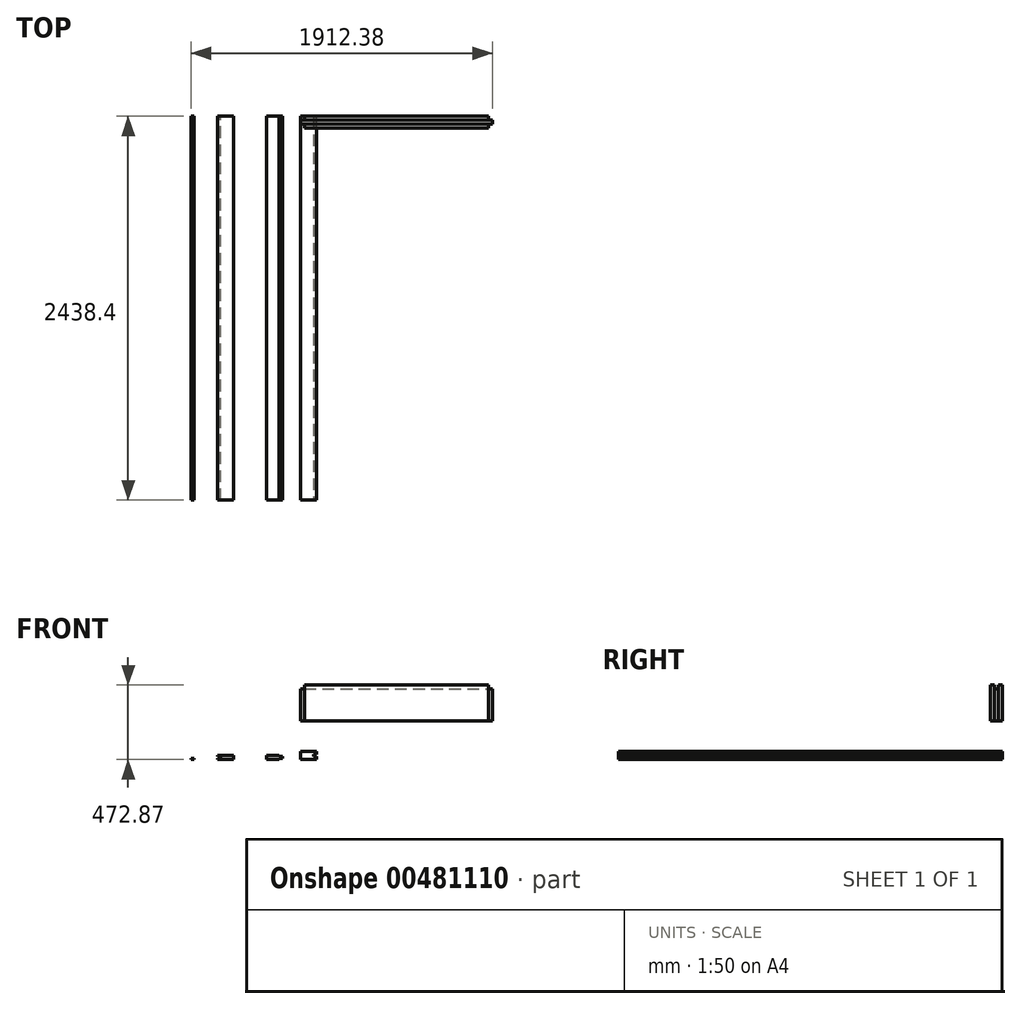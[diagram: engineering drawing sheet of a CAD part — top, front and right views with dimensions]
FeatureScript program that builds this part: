
annotation { "Feature Type Name" : "Feature", "Feature Type Description" : "" }
export const myFeature = defineFeature(function(context is Context, id is Id, definition is map)
    precondition{}
    {
        {
            var Q0;
            Q0=qCreatedBy(makeId("Front.planeOp"),FACE);
            var sketch = newSketch(context, id + "F0", { "sketchPlane" : qUnion([Q0])});
            skLineSegment(sketch, "E0.bottom", {"start": v(0, 0) * mm, "end": v(101.6, 0) * mm});
            skLineSegment(sketch, "E0.top", {"start": v(0, 50.8) * mm, "end": v(101.6, 50.8) * mm});
            skLineSegment(sketch, "E0.left", {"start": v(0, 0) * mm, "end": v(0, 50.8) * mm});
            skLineSegment(sketch, "E0.right", {"start": v(101.6, 0) * mm, "end": v(101.6, 50.8) * mm});
            skSolve(sketch);
        }
        {
            var Q0;
            Q0=makeQuery(id+"F0.imprint","IMPRINT",FACE,{"disambiguationData":[TD([[makeQuery(id+"F0.imprint","IMPRINT",EDGE,{"derivedFrom":sQuery(id+"F0.wireOp",EDGE,"E0.bottom")}),1.0]])]});
            extrude(context, id + "F1", {"entities" : qUnion([Q0]), "depth" : 2438.4 * mm});
        }
        {
            var Q0;
            Q0=makeQuery(id+"F1.opExtrude","SWEPT_FACE",FACE,{"disambiguationData":[OSD([sQuery(id+"F0.wireOp",EDGE,"E0.right")])]});
            var sketch = newSketch(context, id + "F2", { "sketchPlane" : qUnion([Q0])});
            skLineSegment(sketch, "E1.bottom", {"start": v(0, 19.05) * mm, "end": v(-2438.4, 19.05) * mm});
            skLineSegment(sketch, "E1.top", {"start": v(0, 31.75) * mm, "end": v(-2438.4, 31.75) * mm});
            skLineSegment(sketch, "E1.left", {"start": v(0, 19.05) * mm, "end": v(0, 31.75) * mm});
            skLineSegment(sketch, "E1.right", {"start": v(-2438.4, 19.05) * mm, "end": v(-2438.4, 31.75) * mm});
            skSolve(sketch);
        }
        {
            var Q0;
            Q0 = qSketchRegion(id + "F2", true);
            extrude(context, id + "F3", {"entities" : qUnion([Q0]), "operationType" : NewBodyOperationType.REMOVE, "oppositeDirection" : true, "depth" : 19.05 * mm});
        }
        {
            var Q0;
            Q0=qCreatedBy(makeId("Front.planeOp"),FACE);
            var sketch = newSketch(context, id + "F4", { "sketchPlane" : qUnion([Q0])});
            skLineSegment(sketch, "E2.bottom", {"start": v(-114.74, 0) * mm, "end": v(-216.34, 0) * mm});
            skLineSegment(sketch, "E2.top", {"start": v(-114.74, 25.4) * mm, "end": v(-216.34, 25.4) * mm});
            skLineSegment(sketch, "E2.left", {"start": v(-114.74, 0) * mm, "end": v(-114.74, 25.4) * mm});
            skLineSegment(sketch, "E2.right", {"start": v(-216.34, 0) * mm, "end": v(-216.34, 25.4) * mm});
            skSolve(sketch);
        }
        {
            var Q0;
            Q0 = qSketchRegion(id + "F4", true);
            extrude(context, id + "F5", {"entities" : qUnion([Q0]), "depth" : 2438.4 * mm});
        }
        {
            var Q0;
            Q0=makeQuery(id+"F5.opExtrude","CAP_FACE",FACE,{"disambiguationData":[OSD([sQuery(id+"F4.wireOp",EDGE,"E2.bottom"),sQuery(id+"F4.wireOp",EDGE,"E2.top"),sQuery(id+"F4.wireOp",EDGE,"E2.left"),sQuery(id+"F4.wireOp",EDGE,"E2.right")])],"isStart":false});
            var sketch = newSketch(context, id + "F6", { "sketchPlane" : qUnion([Q0])});
            skLineSegment(sketch, "E3.bottom", {"start": v(-114.74, 25.4) * mm, "end": v(-133.8, 25.4) * mm});
            skLineSegment(sketch, "E3.top", {"start": v(-114.74, 19.05) * mm, "end": v(-133.8, 19.05) * mm});
            skLineSegment(sketch, "E3.left", {"start": v(-114.74, 25.4) * mm, "end": v(-114.74, 19.05) * mm});
            skLineSegment(sketch, "E3.right", {"start": v(-133.8, 25.4) * mm, "end": v(-133.8, 19.05) * mm});
            skLineSegment(sketch, "E4.bottom", {"start": v(-114.74, 0) * mm, "end": v(-133.8, 0) * mm});
            skLineSegment(sketch, "E4.top", {"start": v(-114.74, 6.35) * mm, "end": v(-133.8, 6.35) * mm});
            skLineSegment(sketch, "E4.left", {"start": v(-114.74, 0) * mm, "end": v(-114.74, 6.35) * mm});
            skLineSegment(sketch, "E4.right", {"start": v(-133.8, 0) * mm, "end": v(-133.8, 6.35) * mm});
            skSolve(sketch);
        }
        {
            var Q0;
            Q0=makeQuery(id+"F6.imprint","IMPRINT",FACE,{"disambiguationData":[TD([[makeQuery(id+"F6.imprint","IMPRINT",EDGE,{"derivedFrom":sQuery(id+"F6.wireOp",EDGE,"E3.bottom")}),1.0]])]});
            var Q1;
            Q1=makeQuery(id+"F6.imprint","IMPRINT",FACE,{"disambiguationData":[TD([[makeQuery(id+"F6.imprint","IMPRINT",EDGE,{"derivedFrom":sQuery(id+"F6.wireOp",EDGE,"E4.bottom")}),-1.0]])]});
            extrude(context, id + "F7", {"entities" : qUnion([Q0, Q1]), "operationType" : NewBodyOperationType.REMOVE, "oppositeDirection" : true, "depth" : 2438.4 * mm});
        }
        {
            var Q0;
            Q0=qCreatedBy(makeId("Front.planeOp"),FACE);
            var sketch = newSketch(context, id + "F8", { "sketchPlane" : qUnion([Q0])});
            skLineSegment(sketch, "E5.bottom", {"start": v(-423.34, 0) * mm, "end": v(-524.94, 0) * mm});
            skLineSegment(sketch, "E5.top", {"start": v(-423.34, 25.4) * mm, "end": v(-524.94, 25.4) * mm});
            skLineSegment(sketch, "E5.left", {"start": v(-423.34, 0) * mm, "end": v(-423.34, 25.4) * mm});
            skLineSegment(sketch, "E5.right", {"start": v(-524.94, 0) * mm, "end": v(-524.94, 25.4) * mm});
            skLineSegment(sketch, "E6.bottom", {"start": v(-524.94, 19.05) * mm, "end": v(-505.89, 19.05) * mm});
            skLineSegment(sketch, "E6.top", {"start": v(-537.66, 6.35) * mm, "end": v(-505.89, 6.35) * mm});
            skLineSegment(sketch, "E6.right", {"start": v(-505.89, 19.05) * mm, "end": v(-505.89, 6.35) * mm});
            skSolve(sketch);
        }
        {
            var Q0;
            {var subQ1=sQuery(id+"F8.wireOp",EDGE,"E5.bottom");Q0=makeQuery(id+"F8.imprint","IMPRINT",FACE,{"disambiguationData":[TD([[makeQuery(id+"F8.imprint","IMPRINT",EDGE,{"derivedFrom":subQ1}),-1.0]])]});}
            extrude(context, id + "F9", {"entities" : qUnion([Q0]), "depth" : 2438.4 * mm});
        }
        {
            var Q0;
            Q0=qCreatedBy(makeId("Front.planeOp"),FACE);
            var sketch = newSketch(context, id + "F10", { "sketchPlane" : qUnion([Q0])});
            skLineSegment(sketch, "E7.bottom", {"start": v(-674.13, 0) * mm, "end": v(-775.73, 0) * mm});
            skLineSegment(sketch, "E7.top", {"start": v(-674.13, 25.4) * mm, "end": v(-775.73, 25.4) * mm});
            skLineSegment(sketch, "E7.left", {"start": v(-674.13, 0) * mm, "end": v(-674.13, 25.4) * mm});
            skLineSegment(sketch, "E7.right", {"start": v(-775.73, 0) * mm, "end": v(-775.73, 25.4) * mm});
            skLineSegment(sketch, "E8.bottom", {"start": v(-674.13, 25.4) * mm, "end": v(-693.18, 25.4) * mm});
            skLineSegment(sketch, "E8.top", {"start": v(-674.13, 19.05) * mm, "end": v(-693.18, 19.05) * mm});
            skLineSegment(sketch, "E8.left", {"start": v(-674.13, 25.4) * mm, "end": v(-674.13, 19.05) * mm});
            skLineSegment(sketch, "E8.right", {"start": v(-693.18, 25.4) * mm, "end": v(-693.18, 19.05) * mm});
            skLineSegment(sketch, "E9.bottom", {"start": v(-674.13, 0) * mm, "end": v(-693.18, 0) * mm});
            skLineSegment(sketch, "E9.top", {"start": v(-674.13, 6.35) * mm, "end": v(-693.18, 6.35) * mm});
            skLineSegment(sketch, "E9.left", {"start": v(-674.13, 0) * mm, "end": v(-674.13, 6.35) * mm});
            skLineSegment(sketch, "E9.right", {"start": v(-693.18, 0) * mm, "end": v(-693.18, 6.35) * mm});
            skLineSegment(sketch, "E10.bottom", {"start": v(-775.73, 19.05) * mm, "end": v(-756.68, 19.05) * mm});
            skLineSegment(sketch, "E10.top", {"start": v(-775.73, 6.35) * mm, "end": v(-756.68, 6.35) * mm});
            skLineSegment(sketch, "E10.left", {"start": v(-775.73, 19.05) * mm, "end": v(-775.73, 6.35) * mm});
            skLineSegment(sketch, "E10.right", {"start": v(-756.68, 19.05) * mm, "end": v(-756.68, 6.35) * mm});
            skSolve(sketch);
        }
        {
            var Q0;
            {var subQ4=sQuery(id+"F10.wireOp",EDGE,"E7.bottom");Q0=makeQuery(id+"F10.imprint","IMPRINT",FACE,{"disambiguationData":[TD([[makeQuery(id+"F10.imprint","IMPRINT",EDGE,{"derivedFrom":subQ4}),-1.0]])]});}
            extrude(context, id + "F11", {"entities" : qUnion([Q0]), "depth" : 2438.4 * mm});
        }
        {
            var Q0;
            Q0=qCreatedBy(makeId("Front.planeOp"),FACE);
            var sketch = newSketch(context, id + "F12", { "sketchPlane" : qUnion([Q0])});
            skLineSegment(sketch, "E11.bottom", {"start": v(0, 244.27) * mm, "end": v(1219.2, 244.27) * mm});
            skLineSegment(sketch, "E11.top", {"start": v(0, 472.87) * mm, "end": v(1219.2, 472.87) * mm});
            skLineSegment(sketch, "E11.left", {"start": v(0, 244.27) * mm, "end": v(0, 472.87) * mm});
            skLineSegment(sketch, "E11.right", {"start": v(1219.2, 244.27) * mm, "end": v(1219.2, 472.87) * mm});
            skSolve(sketch);
        }
        {
            var Q0;
            Q0 = qSketchRegion(id + "F12", true);
            extrude(context, id + "F13", {"entities" : qUnion([Q0]), "depth" : 76.2 * mm});
        }
        {
            var Q0;
            Q0=makeQuery(id+"F13.opExtrude","SWEPT_FACE",FACE,{"disambiguationData":[OSD([sQuery(id+"F12.wireOp",EDGE,"E11.right")])]});
            var sketch = newSketch(context, id + "F14", { "sketchPlane" : qUnion([Q0])});
            skLineSegment(sketch, "E12.bottom", {"start": v(-50.8, 472.87) * mm, "end": v(-25.4, 472.87) * mm});
            skLineSegment(sketch, "E12.top", {"start": v(-50.8, 447.47) * mm, "end": v(-25.4, 447.47) * mm});
            skLineSegment(sketch, "E12.left", {"start": v(-50.8, 472.87) * mm, "end": v(-50.8, 447.47) * mm});
            skLineSegment(sketch, "E12.right", {"start": v(-25.4, 472.87) * mm, "end": v(-25.4, 447.47) * mm});
            skSolve(sketch);
        }
        {
            var Q0;
            Q0 = qSketchRegion(id + "F14", true);
            extrude(context, id + "F15", {"entities" : qUnion([Q0]), "operationType" : NewBodyOperationType.REMOVE, "oppositeDirection" : true, "depth" : 2438.4 * mm});
        }
        {
            var Q0;
            Q0=makeQuery(id+"F13.opExtrude","CAP_FACE",FACE,{"disambiguationData":[OSD([sQuery(id+"F12.wireOp",EDGE,"E11.bottom"),sQuery(id+"F12.wireOp",EDGE,"E11.top"),sQuery(id+"F12.wireOp",EDGE,"E11.left"),sQuery(id+"F12.wireOp",EDGE,"E11.right")])],"isStart":false});
            var sketch = newSketch(context, id + "F16", { "sketchPlane" : qUnion([Q0])});
            skLineSegment(sketch, "E13.bottom", {"start": v(1219.2, 472.87) * mm, "end": v(1193.8, 472.87) * mm});
            skLineSegment(sketch, "E13.top", {"start": v(1219.2, 244.27) * mm, "end": v(1193.8, 244.27) * mm});
            skLineSegment(sketch, "E13.left", {"start": v(1219.2, 472.87) * mm, "end": v(1219.2, 244.27) * mm});
            skLineSegment(sketch, "E13.right", {"start": v(1193.8, 472.87) * mm, "end": v(1193.8, 244.27) * mm});
            skLineSegment(sketch, "E14.bottom", {"start": v(0, 472.87) * mm, "end": v(25.4, 472.87) * mm});
            skLineSegment(sketch, "E14.top", {"start": v(0, 244.27) * mm, "end": v(25.4, 244.27) * mm});
            skLineSegment(sketch, "E14.left", {"start": v(0, 472.87) * mm, "end": v(0, 244.27) * mm});
            skLineSegment(sketch, "E14.right", {"start": v(25.4, 472.87) * mm, "end": v(25.4, 244.27) * mm});
            skSolve(sketch);
        }
        {
            var Q0;
            Q0 = qSketchRegion(id + "F16", true);
            extrude(context, id + "F17", {"entities" : qUnion([Q0]), "operationType" : NewBodyOperationType.REMOVE, "oppositeDirection" : true, "depth" : 254 * mm});
        }
        {
            var Q0;
            Q0=makeQuery(id+"F17.boolean.opBoolean","COPY",FACE,{"derivedFrom":makeQuery(id+"F17.opExtrude","SWEPT_FACE",FACE,{"disambiguationData":[OSD([sQuery(id+"F16.wireOp",EDGE,"E14.right")])]})});
            var sketch = newSketch(context, id + "F18", { "sketchPlane" : qUnion([Q0])});
            skLineSegment(sketch, "E15.bottom", {"start": v(25.4, 447.47) * mm, "end": v(50.8, 447.47) * mm});
            skLineSegment(sketch, "E15.top", {"start": v(25.4, 244.27) * mm, "end": v(50.8, 244.27) * mm});
            skLineSegment(sketch, "E15.left", {"start": v(25.4, 447.47) * mm, "end": v(25.4, 244.27) * mm});
            skLineSegment(sketch, "E15.right", {"start": v(50.8, 447.47) * mm, "end": v(50.8, 244.27) * mm});
            skSolve(sketch);
        }
        {
            var Q0;
            Q0 = qSketchRegion(id + "F18", true);
            extrude(context, id + "F19", {"entities" : qUnion([Q0]), "operationType" : NewBodyOperationType.ADD, "depth" : 25.4 * mm});
        }
        {
            var Q0;
            Q0=makeQuery(id+"F17.boolean.opBoolean","COPY",FACE,{"derivedFrom":makeQuery(id+"F17.opExtrude","SWEPT_FACE",FACE,{"disambiguationData":[OSD([sQuery(id+"F16.wireOp",EDGE,"E13.right")])]})});
            var sketch = newSketch(context, id + "F20", { "sketchPlane" : qUnion([Q0])});
            skLineSegment(sketch, "E16.bottom", {"start": v(-50.8, 447.47) * mm, "end": v(-25.4, 447.47) * mm});
            skLineSegment(sketch, "E16.top", {"start": v(-50.8, 244.27) * mm, "end": v(-25.4, 244.27) * mm});
            skLineSegment(sketch, "E16.left", {"start": v(-50.8, 447.47) * mm, "end": v(-50.8, 244.27) * mm});
            skLineSegment(sketch, "E16.right", {"start": v(-25.4, 447.47) * mm, "end": v(-25.4, 244.27) * mm});
            skSolve(sketch);
        }
        {
            var Q0;
            Q0 = qSketchRegion(id + "F20", true);
            extrude(context, id + "F21", {"entities" : qUnion([Q0]), "operationType" : NewBodyOperationType.ADD, "depth" : 25.4 * mm});
        }
    });
